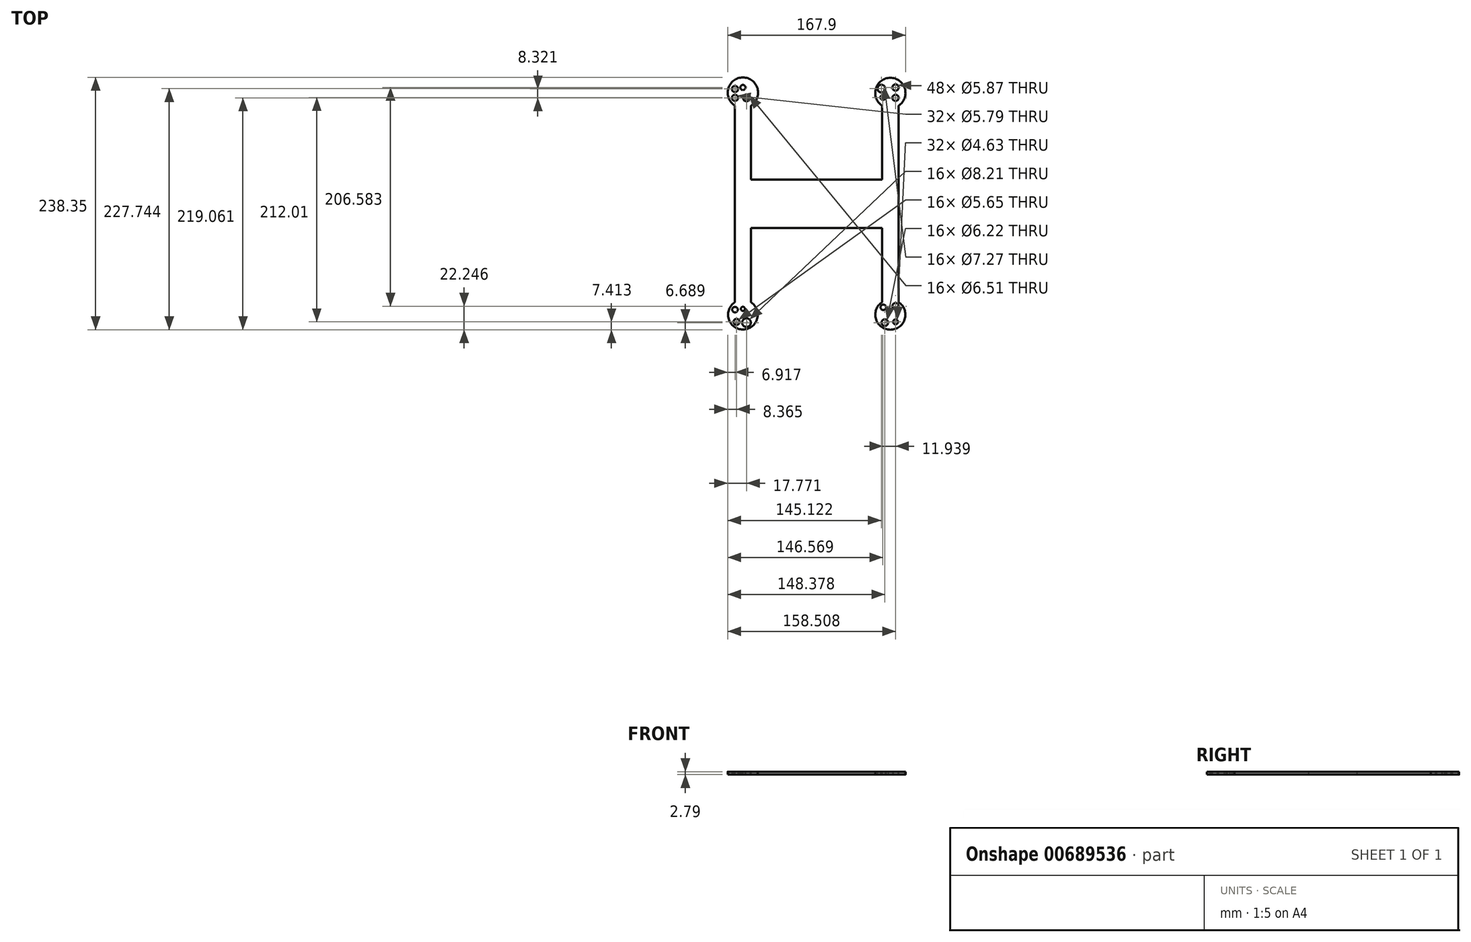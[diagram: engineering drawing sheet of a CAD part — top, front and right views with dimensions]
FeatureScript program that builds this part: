
annotation { "Feature Type Name" : "Feature", "Feature Type Description" : "" }
export const myFeature = defineFeature(function(context is Context, id is Id, definition is map)
    precondition{}
    {
        {
            var Q0;
            Q0=qCreatedBy(makeId("Top.planeOp"),FACE);
            var sketch = newSketch(context, id + "F0", { "sketchPlane" : qUnion([Q0])});
            skLineSegment(sketch, "E0.bottom", {"start": v(77.28, 22.83) * mm, "end": v(-62.28, 22.83) * mm});
            skLineSegment(sketch, "E0.top", {"start": v(77.28, -22.83) * mm, "end": v(-62.28, -22.83) * mm});
            skLineSegment(sketch, "E0.left", {"start": v(77.28, 22.83) * mm, "end": v(77.28, -22.83) * mm});
            skLineSegment(sketch, "E0.right", {"start": v(-77.28, 22.83) * mm, "end": v(-77.28, -22.83) * mm});
            skPoint(sketch, "E0.middle", {"position": v(0, 0) * mm});
            skLineSegment(sketch, "E1.left", {"start": v(-77.28, 22.83) * mm, "end": v(-77.28, 92.83) * mm});
            skLineSegment(sketch, "E1.right", {"start": v(-62.28, 22.83) * mm, "end": v(-62.28, 92.83) * mm});
            skLineSegment(sketch, "E2.left", {"start": v(77.28, 22.83) * mm, "end": v(77.28, 92.83) * mm});
            skLineSegment(sketch, "E2.right", {"start": v(61.63, 22.83) * mm, "end": v(61.63, 92.83) * mm});
            skLineSegment(sketch, "E3.left", {"start": v(-77.28, -22.83) * mm, "end": v(-77.28, -92.83) * mm});
            skLineSegment(sketch, "E3.right", {"start": v(-62.28, -22.83) * mm, "end": v(-62.28, -92.83) * mm});
            skLineSegment(sketch, "E4.left", {"start": v(77.28, -22.83) * mm, "end": v(77.28, -92.83) * mm});
            skLineSegment(sketch, "E4.right", {"start": v(61.63, -22.83) * mm, "end": v(61.63, -92.83) * mm});
            skArc(sketch, "E5", {"start": v(-77.28, -92.83) * mm, "mid": v(-69.78, -118.71) * mm, "end": v(-62.28, -92.83) * mm});
            skPoint(sketch, "E5.third.point", {"position": v(-62.28, -116.54) * mm});
            skArc(sketch, "E6", {"start": v(61.63, -92.83) * mm, "mid": v(69.46, -118.9) * mm, "end": v(77.28, -92.83) * mm});
            skPoint(sketch, "E6.third.point", {"position": v(77.28, -116.54) * mm});
            skArc(sketch, "E7", {"start": v(-62.28, 92.83) * mm, "mid": v(-69.78, 119.46) * mm, "end": v(-77.28, 92.83) * mm});
            skPoint(sketch, "E7.third.point", {"position": v(-83.03, 110.66) * mm});
            skArc(sketch, "E8", {"start": v(77.28, 92.83) * mm, "mid": v(69.46, 119.07) * mm, "end": v(61.63, 92.83) * mm});
            skPoint(sketch, "E8.third.point", {"position": v(55.17, 105.09) * mm});
            skCircle(sketch, "E9", {"center": v(62.4, 100.53) * mm, "radius": 2.32 * mm});
            skCircle(sketch, "E10", {"center": v(74.35, 100.17) * mm, "radius": 2.93 * mm});
            skCircle(sketch, "E11", {"center": v(60.96, 108.85) * mm, "radius": 3.64 * mm});
            skCircle(sketch, "E12", {"center": v(74.35, 109.94) * mm, "radius": 2.93 * mm});
            skCircle(sketch, "E13", {"center": v(62.77, -97.73) * mm, "radius": 2.56 * mm});
            skCircle(sketch, "E14", {"center": v(74.35, -96.64) * mm, "radius": 2.93 * mm});
            skCircle(sketch, "E15", {"center": v(74.35, -111.48) * mm, "radius": 2.32 * mm});
            skCircle(sketch, "E16", {"center": v(64.22, -112.2) * mm, "radius": 3.11 * mm});
            skCircle(sketch, "E17", {"center": v(-77.24, -99.9) * mm, "radius": 2.63 * mm});
            skCircle(sketch, "E18", {"center": v(-69.78, -99.18) * mm, "radius": 1.98 * mm});
            skCircle(sketch, "E19", {"center": v(-75.8, -111.48) * mm, "radius": 2.83 * mm});
            skCircle(sketch, "E20", {"center": v(-66.39, -112.2) * mm, "radius": 4.1 * mm});
            skCircle(sketch, "E21", {"center": v(-77.24, 108.5) * mm, "radius": 2.9 * mm});
            skCircle(sketch, "E22", {"center": v(-69.78, 109.94) * mm, "radius": 2.43 * mm});
            skCircle(sketch, "E23", {"center": v(-77.24, 100.17) * mm, "radius": 2.9 * mm});
            skCircle(sketch, "E24", {"center": v(-66.39, 100.17) * mm, "radius": 3.26 * mm});
            skSolve(sketch);
        }
        {
            var Q0;
            Q0 = qSketchRegion(id + "F0", true);
            extrude(context, id + "F1", {"entities" : qUnion([Q0]), "depth" : 2.8 * mm, "offsetDistance" : 25.4 * mm});
        }
    });
